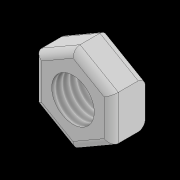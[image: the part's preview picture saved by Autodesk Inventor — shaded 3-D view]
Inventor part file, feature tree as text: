
AUTODESK INVENTOR PART (.ipt)
format: ipt  version: 2022.2 (Build 262287010, 287A)  size: 111,104 bytes
history: native  units: mm
features: extrude x1, thread x1, fillet x1, sketch x1
ambient origin geometry x8: Origin, YZ Plane, XZ Plane, XY Plane, X Axis, Y Axis, Z Axis, Center Point
bodies: Solid1 (feature_tree)
feature tree (4):
  extrude  "Extrusion1"  Depth=1.5mm
  thread  "Thread1"  [1 undecoded]
  fillet  "Fillet1"  [1 undecoded]
  sketch  "Sketch1"  dims[d0=5.4mm d1=1.5mm d2=2.4mm d3=0.0mm d4=2.4mm d5=0.0mm d6=0.5mm]
note: 2 required parameter values undecoded (feature->parameter linkage not recoverable at this tier; creation-order binding heuristic only, values carry confidence <= 0.55)
